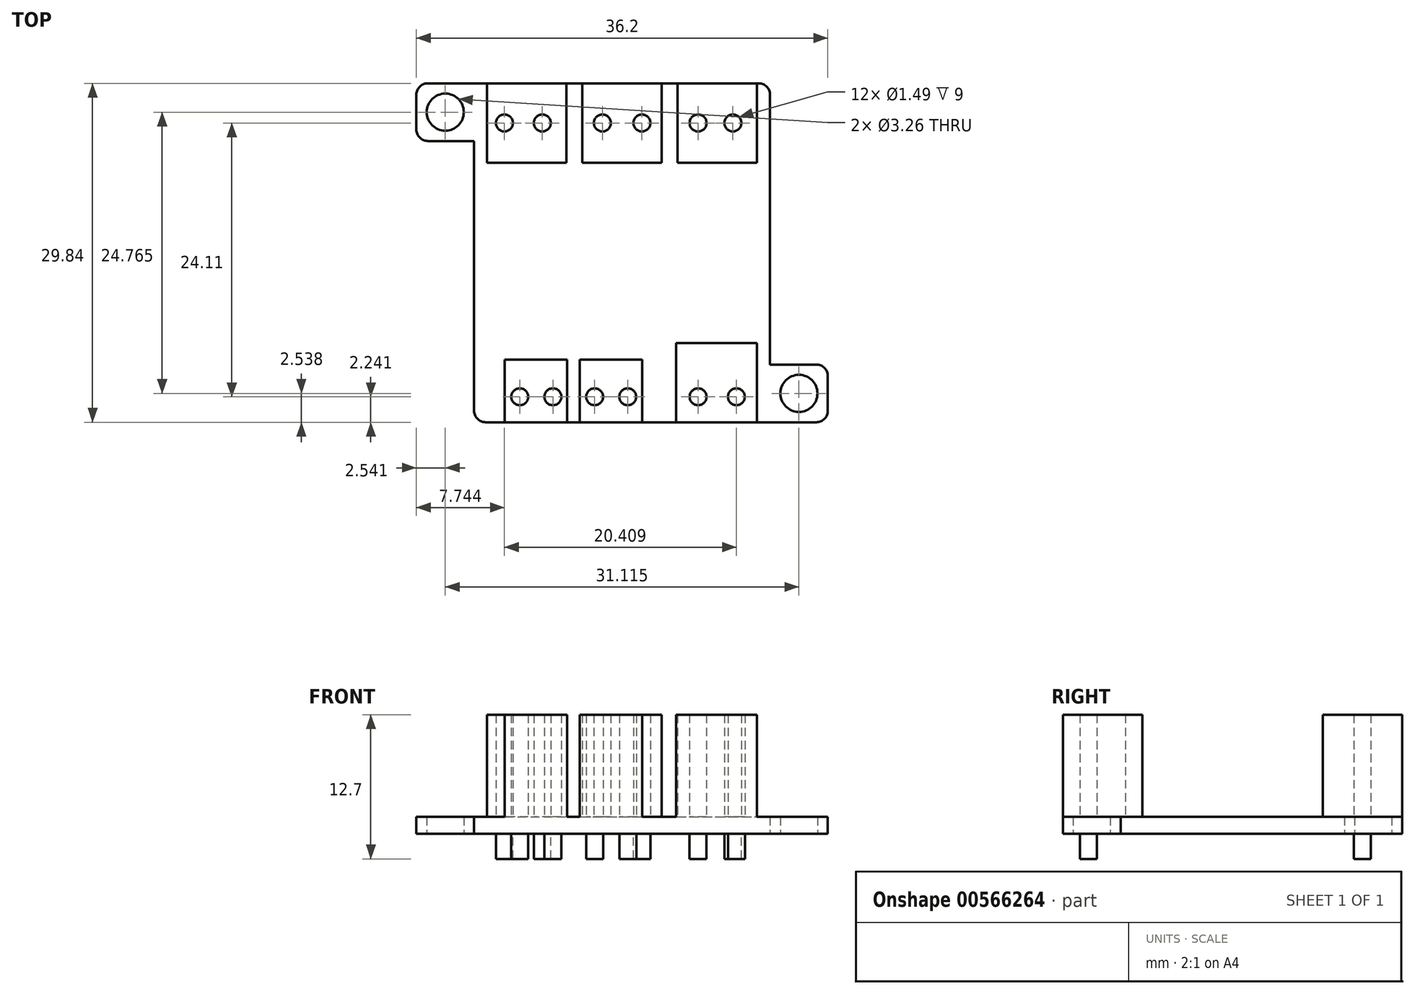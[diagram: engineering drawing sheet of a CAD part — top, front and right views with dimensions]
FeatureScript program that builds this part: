
annotation { "Feature Type Name" : "Feature", "Feature Type Description" : "" }
export const myFeature = defineFeature(function(context is Context, id is Id, definition is map)
    precondition{}
    {
        {
            var Q0;
            Q0=qCreatedBy(makeId("Top.planeOp"),FACE);
            var sketch = newSketch(context, id + "F0", { "sketchPlane" : qUnion([Q0])});
            skLineSegment(sketch, "E0", {"start": v(-28.66, 22.43) * mm, "end": v(0.46, 22.43) * mm});
            skLineSegment(sketch, "E1", {"start": v(1.46, 21.43) * mm, "end": v(1.46, -2.33) * mm});
            skLineSegment(sketch, "E2", {"start": v(1.46, -2.33) * mm, "end": v(5.54, -2.33) * mm});
            skLineSegment(sketch, "E3", {"start": v(6.54, -3.33) * mm, "end": v(6.54, -6.41) * mm});
            skLineSegment(sketch, "E4", {"start": v(5.54, -7.41) * mm, "end": v(-23.58, -7.41) * mm});
            skLineSegment(sketch, "E5", {"start": v(-24.58, -6.41) * mm, "end": v(-24.58, 17.35) * mm});
            skLineSegment(sketch, "E6", {"start": v(-24.58, 17.35) * mm, "end": v(-28.66, 17.35) * mm});
            skLineSegment(sketch, "E7", {"start": v(-29.66, 18.35) * mm, "end": v(-29.66, 21.43) * mm});
            skCircle(sketch, "E8", {"center": v(-27.12, 19.9) * mm, "radius": 1.63 * mm});
            skCircle(sketch, "E9", {"center": v(4, -4.87) * mm, "radius": 1.63 * mm});
            skLineSegment(sketch, "E10", {"start": v(4, -2.33) * mm, "end": v(4, -7.41) * mm, "construction": true});
            skLineSegment(sketch, "E11", {"start": v(-27.12, 17.35) * mm, "end": v(-27.12, 22.43) * mm, "construction": true});
            skPoint(sketch, "E12.visualSharp", {"position": v(-29.66, 22.43) * mm});
            skArc(sketch, "E12.filletArc", {"start": v(-28.66, 22.43) * mm, "mid": v(-29.37, 22.14) * mm, "end": v(-29.66, 21.43) * mm});
            skPoint(sketch, "E13.visualSharp", {"position": v(-29.66, 17.35) * mm});
            skArc(sketch, "E13.filletArc", {"start": v(-29.66, 18.35) * mm, "mid": v(-29.37, 17.65) * mm, "end": v(-28.66, 17.35) * mm});
            skPoint(sketch, "E14.visualSharp", {"position": v(6.54, -7.41) * mm});
            skArc(sketch, "E14.filletArc", {"start": v(5.54, -7.41) * mm, "mid": v(6.24, -7.12) * mm, "end": v(6.54, -6.41) * mm});
            skPoint(sketch, "E15.visualSharp", {"position": v(6.54, -2.33) * mm});
            skArc(sketch, "E15.filletArc", {"start": v(6.54, -3.33) * mm, "mid": v(6.24, -2.62) * mm, "end": v(5.54, -2.33) * mm});
            skPoint(sketch, "E16.visualSharp", {"position": v(-24.58, -7.41) * mm});
            skArc(sketch, "E16.filletArc", {"start": v(-24.58, -6.41) * mm, "mid": v(-24.29, -7.12) * mm, "end": v(-23.58, -7.41) * mm});
            skPoint(sketch, "E17.visualSharp", {"position": v(1.46, 22.43) * mm});
            skArc(sketch, "E17.filletArc", {"start": v(1.46, 21.43) * mm, "mid": v(1.16, 22.14) * mm, "end": v(0.46, 22.43) * mm});
            skSolve(sketch);
        }
        {
            var Q0;
            Q0=makeQuery(id+"F0.imprint","IMPRINT",FACE,{"disambiguationData":[TD([[makeQuery(id+"F0.imprint","IMPRINT",EDGE,{"derivedFrom":sQuery(id+"F0.wireOp",EDGE,"E0")}),-1.0]])]});
            extrude(context, id + "F1", {"entities" : qUnion([Q0]), "depth" : 1.5 * mm, "offsetDistance" : 25 * mm});
        }
        {
            var Q0;
            Q0=makeQuery(id+"F1.opExtrude","CAP_FACE",FACE,{"disambiguationData":[OSD([sQuery(id+"F0.wireOp",EDGE,"E0"),sQuery(id+"F0.wireOp",EDGE,"E1"),sQuery(id+"F0.wireOp",EDGE,"E2"),sQuery(id+"F0.wireOp",EDGE,"E3"),sQuery(id+"F0.wireOp",EDGE,"E4"),sQuery(id+"F0.wireOp",EDGE,"E5"),sQuery(id+"F0.wireOp",EDGE,"E6"),sQuery(id+"F0.wireOp",EDGE,"E7"),sQuery(id+"F0.wireOp",EDGE,"E8"),sQuery(id+"F0.wireOp",EDGE,"E9"),sQuery(id+"F0.wireOp",EDGE,"E12.filletArc"),sQuery(id+"F0.wireOp",EDGE,"E13.filletArc"),sQuery(id+"F0.wireOp",EDGE,"E14.filletArc"),sQuery(id+"F0.wireOp",EDGE,"E15.filletArc"),sQuery(id+"F0.wireOp",EDGE,"E16.filletArc"),sQuery(id+"F0.wireOp",EDGE,"E17.filletArc")])],"isStart":false});
            var sketch = newSketch(context, id + "F2", { "sketchPlane" : qUnion([Q0])});
            skLineSegment(sketch, "E18.bottom", {"start": v(-23.44, 22.43) * mm, "end": v(-16.45, 22.43) * mm});
            skLineSegment(sketch, "E18.top", {"start": v(-23.44, 15.45) * mm, "end": v(-16.45, 15.45) * mm});
            skLineSegment(sketch, "E18.left", {"start": v(-23.44, 22.43) * mm, "end": v(-23.44, 15.45) * mm});
            skLineSegment(sketch, "E18.right", {"start": v(-16.45, 22.43) * mm, "end": v(-16.45, 15.45) * mm});
            skLineSegment(sketch, "E19.1.0.0", {"start": v(-8.07, 22.43) * mm, "end": v(-8.07, 15.45) * mm});
            skLineSegment(sketch, "E19.1.0.1", {"start": v(-15.05, 15.45) * mm, "end": v(-8.07, 15.45) * mm});
            skLineSegment(sketch, "E19.1.0.2", {"start": v(-15.05, 22.43) * mm, "end": v(-15.05, 15.45) * mm});
            skLineSegment(sketch, "E19.1.0.3", {"start": v(-15.05, 22.43) * mm, "end": v(-8.07, 22.43) * mm});
            skLineSegment(sketch, "E19.2.0.0", {"start": v(0.31, 22.43) * mm, "end": v(0.31, 15.45) * mm});
            skLineSegment(sketch, "E19.2.0.1", {"start": v(-6.67, 15.45) * mm, "end": v(0.31, 15.45) * mm});
            skLineSegment(sketch, "E19.2.0.2", {"start": v(-6.67, 22.43) * mm, "end": v(-6.67, 15.45) * mm});
            skLineSegment(sketch, "E19.2.0.3", {"start": v(-6.67, 22.43) * mm, "end": v(0.31, 22.43) * mm});
            skLineSegment(sketch, "E19.direction1", {"start": v(-16.45, 15.45) * mm, "end": v(-8.07, 15.45) * mm, "construction": true});
            skLineSegment(sketch, "E20", {"start": v(-23.44, 16.48) * mm, "end": v(-24.58, 16.48) * mm, "construction": true});
            skLineSegment(sketch, "E21", {"start": v(0.31, 16.6) * mm, "end": v(1.46, 16.6) * mm, "construction": true});
            skLineSegment(sketch, "E22.0.1.0", {"start": v(0.31, -0.43) * mm, "end": v(0.31, -7.41) * mm});
            skLineSegment(sketch, "E22.0.1.1", {"start": v(-6.83, -7.41) * mm, "end": v(0.31, -7.41) * mm});
            skLineSegment(sketch, "E22.0.1.2", {"start": v(-6.83, -0.43) * mm, "end": v(-6.83, -7.41) * mm});
            skLineSegment(sketch, "E22.0.1.3", {"start": v(-6.83, -0.43) * mm, "end": v(0.31, -0.43) * mm});
            skLineSegment(sketch, "E22.direction2", {"start": v(0.31, 15.45) * mm, "end": v(0.31, -7.41) * mm, "construction": true});
            skLineSegment(sketch, "E23.bottom", {"start": v(-21.89, -1.91) * mm, "end": v(-16.39, -1.91) * mm});
            skLineSegment(sketch, "E23.top", {"start": v(-21.89, -7.41) * mm, "end": v(-16.39, -7.41) * mm});
            skLineSegment(sketch, "E23.left", {"start": v(-21.89, -1.91) * mm, "end": v(-21.89, -7.41) * mm});
            skLineSegment(sketch, "E23.right", {"start": v(-16.39, -1.91) * mm, "end": v(-16.39, -7.41) * mm});
            skCircle(sketch, "E24", {"center": v(-20.56, -5.17) * mm, "radius": 0.75 * mm});
            skCircle(sketch, "E25", {"center": v(-17.65, -5.17) * mm, "radius": 0.75 * mm});
            skLineSegment(sketch, "E26.1.0.0", {"start": v(-15.3, -1.91) * mm, "end": v(-15.3, -7.41) * mm});
            skLineSegment(sketch, "E26.1.0.1", {"start": v(-15.3, -1.91) * mm, "end": v(-9.8, -1.91) * mm});
            skLineSegment(sketch, "E26.1.0.2", {"start": v(-9.8, -1.91) * mm, "end": v(-9.8, -7.41) * mm});
            skLineSegment(sketch, "E26.1.0.3", {"start": v(-15.3, -7.41) * mm, "end": v(-9.8, -7.41) * mm});
            skCircle(sketch, "E26.1.0.4", {"center": v(-11.06, -5.17) * mm, "radius": 0.75 * mm});
            skCircle(sketch, "E26.1.0.5", {"center": v(-13.98, -5.17) * mm, "radius": 0.75 * mm});
            skLineSegment(sketch, "E26.direction1", {"start": v(-21.89, -7.41) * mm, "end": v(-15.3, -7.41) * mm, "construction": true});
            skCircle(sketch, "E27", {"center": v(-4.88, -5.17) * mm, "radius": 0.75 * mm});
            skCircle(sketch, "E28", {"center": v(-1.5, -5.17) * mm, "radius": 0.75 * mm});
            skCircle(sketch, "E29", {"center": v(-21.92, 18.94) * mm, "radius": 0.75 * mm});
            skPoint(sketch, "E29.centerSnap0", {"position": v(-23.44, 18.94) * mm});
            skCircle(sketch, "E30", {"center": v(-18.58, 18.94) * mm, "radius": 0.75 * mm});
            skCircle(sketch, "E31", {"center": v(-13.3, 18.94) * mm, "radius": 0.75 * mm});
            skCircle(sketch, "E32", {"center": v(-9.82, 18.94) * mm, "radius": 0.75 * mm});
            skCircle(sketch, "E33", {"center": v(-4.87, 18.94) * mm, "radius": 0.75 * mm});
            skCircle(sketch, "E34", {"center": v(-1.82, 18.94) * mm, "radius": 0.75 * mm});
            skLineSegment(sketch, "E35", {"start": v(-21.92, 15.45) * mm, "end": v(-21.92, 22.43) * mm, "construction": true});
            skSolve(sketch);
        }
        {
            var Q0;
            Q0=makeQuery(id+"F2.imprint","IMPRINT",FACE,{"disambiguationData":[TD([[makeQuery(id+"F2.imprint","IMPRINT",EDGE,{"derivedFrom":sQuery(id+"F2.wireOp",EDGE,"E18.bottom")}),-1.0]])]});
            var Q1;
            Q1=makeQuery(id+"F2.imprint","IMPRINT",FACE,{"disambiguationData":[TD([[makeQuery(id+"F2.imprint","IMPRINT",EDGE,{"derivedFrom":sQuery(id+"F2.wireOp",EDGE,"E19.1.0.0")}),-1.0]])]});
            var Q2;
            Q2=makeQuery(id+"F2.imprint","IMPRINT",FACE,{"disambiguationData":[TD([[makeQuery(id+"F2.imprint","IMPRINT",EDGE,{"derivedFrom":sQuery(id+"F2.wireOp",EDGE,"E19.2.0.0")}),-1.0]])]});
            var Q3;
            Q3=makeQuery(id+"F2.imprint","IMPRINT",FACE,{"disambiguationData":[TD([[makeQuery(id+"F2.imprint","IMPRINT",EDGE,{"derivedFrom":sQuery(id+"F2.wireOp",EDGE,"E22.0.1.0")}),-1.0]])]});
            var Q4;
            Q4=makeQuery(id+"F2.imprint","IMPRINT",FACE,{"disambiguationData":[TD([[makeQuery(id+"F2.imprint","IMPRINT",EDGE,{"derivedFrom":sQuery(id+"F2.wireOp",EDGE,"E26.1.0.0")}),1.0]])]});
            var Q5;
            Q5=makeQuery(id+"F2.imprint","IMPRINT",FACE,{"disambiguationData":[TD([[makeQuery(id+"F2.imprint","IMPRINT",EDGE,{"derivedFrom":sQuery(id+"F2.wireOp",EDGE,"E23.bottom")}),-1.0]])]});
            extrude(context, id + "F3", {"entities" : qUnion([Q0, Q1, Q2, Q3, Q4, Q5]), "operationType" : NewBodyOperationType.ADD, "depth" : 9 * mm, "offsetDistance" : 25 * mm});
        }
        {
            var Q0;
            Q0=makeQuery(id+"F2.imprint","IMPRINT",FACE,{"disambiguationData":[TD([[makeQuery(id+"F2.imprint","IMPRINT",EDGE,{"derivedFrom":sQuery(id+"F2.wireOp",EDGE,"E24")}),1.0]])]});
            var Q1;
            Q1=makeQuery(id+"F2.imprint","IMPRINT",FACE,{"disambiguationData":[TD([[makeQuery(id+"F2.imprint","IMPRINT",EDGE,{"derivedFrom":sQuery(id+"F2.wireOp",EDGE,"E26.1.0.5")}),1.0]])]});
            var Q2;
            Q2=makeQuery(id+"F2.imprint","IMPRINT",FACE,{"disambiguationData":[TD([[makeQuery(id+"F2.imprint","IMPRINT",EDGE,{"derivedFrom":sQuery(id+"F2.wireOp",EDGE,"E25")}),1.0]])]});
            var Q3;
            Q3=makeQuery(id+"F2.imprint","IMPRINT",FACE,{"disambiguationData":[TD([[makeQuery(id+"F2.imprint","IMPRINT",EDGE,{"derivedFrom":sQuery(id+"F2.wireOp",EDGE,"E26.1.0.4")}),1.0]])]});
            var Q4;
            Q4=makeQuery(id+"F2.imprint","IMPRINT",FACE,{"disambiguationData":[TD([[makeQuery(id+"F2.imprint","IMPRINT",EDGE,{"derivedFrom":sQuery(id+"F2.wireOp",EDGE,"E27")}),1.0]])]});
            var Q5;
            Q5=makeQuery(id+"F2.imprint","IMPRINT",FACE,{"disambiguationData":[TD([[makeQuery(id+"F2.imprint","IMPRINT",EDGE,{"derivedFrom":sQuery(id+"F2.wireOp",EDGE,"E28")}),1.0]])]});
            var Q6;
            Q6=makeQuery(id+"F2.imprint","IMPRINT",FACE,{"disambiguationData":[TD([[makeQuery(id+"F2.imprint","IMPRINT",EDGE,{"derivedFrom":sQuery(id+"F2.wireOp",EDGE,"E34")}),1.0]])]});
            var Q7;
            Q7=makeQuery(id+"F2.imprint","IMPRINT",FACE,{"disambiguationData":[TD([[makeQuery(id+"F2.imprint","IMPRINT",EDGE,{"derivedFrom":sQuery(id+"F2.wireOp",EDGE,"E33")}),1.0]])]});
            var Q8;
            Q8=makeQuery(id+"F2.imprint","IMPRINT",FACE,{"disambiguationData":[TD([[makeQuery(id+"F2.imprint","IMPRINT",EDGE,{"derivedFrom":sQuery(id+"F2.wireOp",EDGE,"E32")}),1.0]])]});
            var Q9;
            Q9=makeQuery(id+"F2.imprint","IMPRINT",FACE,{"disambiguationData":[TD([[makeQuery(id+"F2.imprint","IMPRINT",EDGE,{"derivedFrom":sQuery(id+"F2.wireOp",EDGE,"E30")}),1.0]])]});
            var Q10;
            Q10=makeQuery(id+"F2.imprint","IMPRINT",FACE,{"disambiguationData":[TD([[makeQuery(id+"F2.imprint","IMPRINT",EDGE,{"derivedFrom":sQuery(id+"F2.wireOp",EDGE,"E29")}),1.0]])]});
            extrude(context, id + "F4", {"entities" : qUnion([Q0, Q1, Q2, Q3, Q4, Q5, Q6, Q7, Q8, Q9, Q10]), "operationType" : NewBodyOperationType.ADD, "oppositeDirection" : true, "depth" : 3.7 * mm, "offsetDistance" : 25 * mm});
        }
    });
